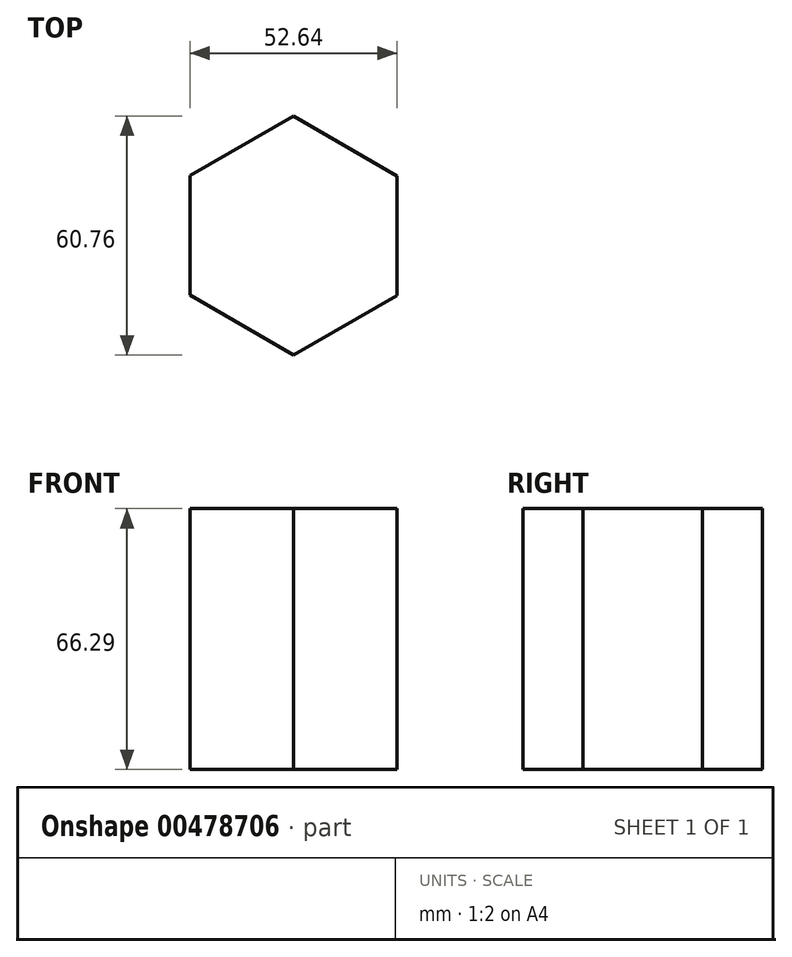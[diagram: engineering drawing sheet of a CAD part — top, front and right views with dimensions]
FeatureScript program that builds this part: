
annotation { "Feature Type Name" : "Feature", "Feature Type Description" : "" }
export const myFeature = defineFeature(function(context is Context, id is Id, definition is map)
    precondition{}
    {
        {
            var Q0;
            Q0=qCreatedBy(makeId("Top.planeOp"),FACE);
            var sketch = newSketch(context, id + "F0", { "sketchPlane" : qUnion([Q0])});
            skCircle(sketch, "E0.cCircle", {"center": v(0, 0) * mm, "radius": 26.3 * mm, "construction": true});
            skLineSegment(sketch, "E0.0", {"start": v(0.03, 30.38) * mm, "end": v(26.32, 15.16) * mm});
            skLineSegment(sketch, "E0.1", {"start": v(26.32, 15.16) * mm, "end": v(26.3, -15.21) * mm});
            skLineSegment(sketch, "E0.2", {"start": v(26.3, -15.21) * mm, "end": v(-0.03, -30.38) * mm});
            skLineSegment(sketch, "E0.3", {"start": v(-0.03, -30.38) * mm, "end": v(-26.32, -15.16) * mm});
            skLineSegment(sketch, "E0.4", {"start": v(-26.32, -15.16) * mm, "end": v(-26.3, 15.21) * mm});
            skLineSegment(sketch, "E0.5", {"start": v(-26.3, 15.21) * mm, "end": v(0.03, 30.38) * mm});
            skPoint(sketch, "E0.0.midPoint", {"position": v(13.18, 22.77) * mm});
            skSolve(sketch);
        }
        {
            var Q0;
            Q0 = qSketchRegion(id + "F0", true);
            extrude(context, id + "F1", {"entities" : qUnion([Q0]), "depth" : 66.3 * mm});
        }
    });
